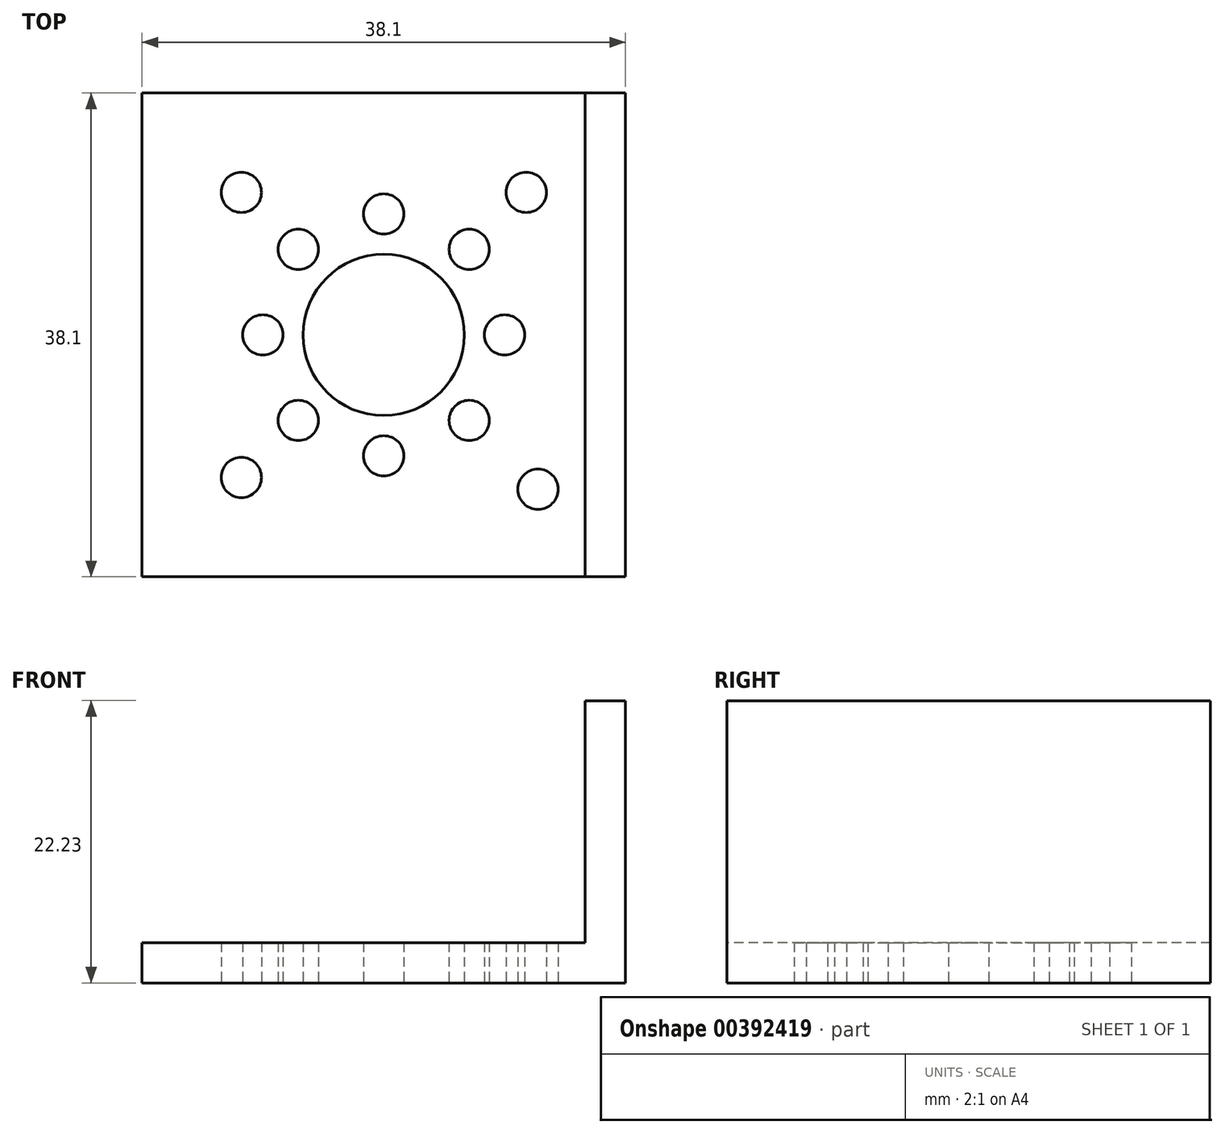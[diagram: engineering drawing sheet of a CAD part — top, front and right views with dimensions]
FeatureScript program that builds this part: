
annotation { "Feature Type Name" : "Feature", "Feature Type Description" : "" }
export const myFeature = defineFeature(function(context is Context, id is Id, definition is map)
    precondition{}
    {
        {
            var Q0;
            Q0=qCreatedBy(makeId("Top.planeOp"),FACE);
            var sketch = newSketch(context, id + "F0", { "sketchPlane" : qUnion([Q0])});
            skLineSegment(sketch, "E0.bottom", {"start": v(-38.1, 48.74) * mm, "end": v(0, 48.74) * mm});
            skLineSegment(sketch, "E0.top", {"start": v(-38.1, 10.64) * mm, "end": v(0, 10.64) * mm});
            skLineSegment(sketch, "E0.left", {"start": v(-38.1, 48.74) * mm, "end": v(-38.1, 10.64) * mm});
            skLineSegment(sketch, "E0.right", {"start": v(0, 48.74) * mm, "end": v(0, 10.64) * mm});
            skLineSegment(sketch, "E1.bottom", {"start": v(0, 48.74) * mm, "end": v(0, 48.74) * mm});
            skLineSegment(sketch, "E1.top", {"start": v(0, 10.64) * mm, "end": v(0, 10.64) * mm});
            skLineSegment(sketch, "E2.left", {"start": v(0, 10.64) * mm, "end": v(0, 48.74) * mm});
            skCircle(sketch, "E3", {"center": v(-19.05, 29.7) * mm, "radius": 6.35 * mm});
            skCircle(sketch, "E4", {"center": v(-19.05, 20.17) * mm, "radius": 1.59 * mm});
            skPoint(sketch, "E5", {"position": v(-19.05, 10.64) * mm});
            skPoint(sketch, "E6", {"position": v(-19.05, 48.74) * mm});
            skPoint(sketch, "E7", {"position": v(-38.1, 29.7) * mm});
            skPoint(sketch, "E8", {"position": v(0, 29.7) * mm});
            skLineSegment(sketch, "E9", {"start": v(-19.05, 10.64) * mm, "end": v(-19.05, 48.74) * mm});
            skLineSegment(sketch, "E10", {"start": v(0, 29.7) * mm, "end": v(-38.1, 29.7) * mm});
            skLineSegment(sketch, "E11", {"start": v(-38.1, 48.74) * mm, "end": v(0, 10.64) * mm});
            skLineSegment(sketch, "E12", {"start": v(0, 48.74) * mm, "end": v(-38.1, 10.64) * mm});
            skPoint(sketch, "E13", {"position": v(-19.05, 23.34) * mm});
            skPoint(sketch, "E14", {"position": v(-19.05, 36.04) * mm});
            skCircle(sketch, "E15", {"center": v(-19.05, 39.22) * mm, "radius": 1.59 * mm});
            skCircle(sketch, "E16", {"center": v(-28.58, 29.7) * mm, "radius": 1.59 * mm});
            skCircle(sketch, "E17", {"center": v(-9.53, 29.7) * mm, "radius": 1.59 * mm});
            skCircle(sketch, "E18", {"center": v(-25.79, 22.96) * mm, "radius": 1.59 * mm});
            skCircle(sketch, "E19", {"center": v(-12.31, 36.43) * mm, "radius": 1.59 * mm});
            skCircle(sketch, "E20", {"center": v(-25.79, 36.43) * mm, "radius": 1.59 * mm});
            skCircle(sketch, "E21", {"center": v(-12.31, 22.96) * mm, "radius": 1.59 * mm});
            skCircle(sketch, "E22", {"center": v(-30.28, 18.47) * mm, "radius": 1.59 * mm});
            skCircle(sketch, "E23", {"center": v(-6.9, 17.54) * mm, "radius": 1.59 * mm});
            skCircle(sketch, "E24", {"center": v(-30.28, 40.92) * mm, "radius": 1.59 * mm});
            skCircle(sketch, "E25", {"center": v(-7.82, 40.92) * mm, "radius": 1.59 * mm});
            skPoint(sketch, "E26", {"position": v(-23.54, 25.2) * mm});
            skPoint(sketch, "E27", {"position": v(-14.56, 25.2) * mm});
            skPoint(sketch, "E28", {"position": v(-25.4, 29.7) * mm});
            skPoint(sketch, "E29", {"position": v(-23.54, 34.18) * mm});
            skPoint(sketch, "E30", {"position": v(-14.56, 34.18) * mm});
            skPoint(sketch, "E31", {"position": v(-12.7, 29.7) * mm});
            skPoint(sketch, "E32", {"position": v(-26.9, 21.83) * mm});
            skPoint(sketch, "E33", {"position": v(-29.15, 19.59) * mm});
            skPoint(sketch, "E34", {"position": v(-11.2, 21.83) * mm});
            skPoint(sketch, "E35", {"position": v(-8.02, 18.66) * mm});
            skPoint(sketch, "E36", {"position": v(-11.2, 37.55) * mm});
            skPoint(sketch, "E37", {"position": v(-8.95, 39.8) * mm});
            skPoint(sketch, "E38", {"position": v(-29.15, 39.8) * mm});
            skPoint(sketch, "E39", {"position": v(-26.9, 37.55) * mm});
            skPoint(sketch, "E2.right.end.orphan", {"position": v(3.17, 48.74) * mm});
            skSolve(sketch);
        }
        {
            var Q0;
            {var subQ0=sQuery(id+"F0.wireOp",EDGE,"E10");var subQ1=sQuery(id+"F0.wireOp",EDGE,"E3");var subQ2=makeQuery(id+"F0.imprint","INTERSECT",VERTEX,{"disambiguationData":[OD(0.0)],"derivedFrom":[subQ1,subQ0]});Q0=makeQuery(id+"F0.imprint","IMPRINT",FACE,{"disambiguationData":[TD([[makeQuery(id+"F0.imprint","IMPRINT",EDGE,{"disambiguationData":[TD([[subQ2,1.0]])],"derivedFrom":subQ1}),-1.0]])]});}
            var Q1;
            {var subQ0=sQuery(id+"F0.wireOp",EDGE,"E9");var subQ6=sQuery(id+"F0.wireOp",EDGE,"E3");var subQ7=makeQuery(id+"F0.imprint","INTERSECT",VERTEX,{"disambiguationData":[OD(1.0)],"derivedFrom":[subQ6,subQ0]});Q1=makeQuery(id+"F0.imprint","IMPRINT",FACE,{"disambiguationData":[TD([[makeQuery(id+"F0.imprint","IMPRINT",EDGE,{"disambiguationData":[TD([[subQ7,-1.0]])],"derivedFrom":subQ6}),-1.0]])]});}
            var Q2;
            {var subQ7=sQuery(id+"F0.wireOp",EDGE,"E12");var subQ10=sQuery(id+"F0.wireOp",EDGE,"E3");var subQ11=makeQuery(id+"F0.imprint","INTERSECT",VERTEX,{"disambiguationData":[OD(1.0)],"derivedFrom":[subQ10,subQ7]});Q2=makeQuery(id+"F0.imprint","IMPRINT",FACE,{"disambiguationData":[TD([[makeQuery(id+"F0.imprint","IMPRINT",EDGE,{"disambiguationData":[TD([[subQ11,-1.0]])],"derivedFrom":subQ10}),-1.0]])]});}
            var Q3;
            {var subQ0=sQuery(id+"F0.wireOp",EDGE,"E10");var subQ10=sQuery(id+"F0.wireOp",EDGE,"E3");var subQ11=makeQuery(id+"F0.imprint","INTERSECT",VERTEX,{"disambiguationData":[OD(1.0)],"derivedFrom":[subQ10,subQ0]});Q3=makeQuery(id+"F0.imprint","IMPRINT",FACE,{"disambiguationData":[TD([[makeQuery(id+"F0.imprint","IMPRINT",EDGE,{"disambiguationData":[TD([[subQ11,-1.0]])],"derivedFrom":subQ10}),-1.0]])]});}
            var Q4;
            {var subQ5=sQuery(id+"F0.wireOp",EDGE,"E11");var subQ6=sQuery(id+"F0.wireOp",EDGE,"E3");var subQ7=makeQuery(id+"F0.imprint","INTERSECT",VERTEX,{"disambiguationData":[OD(0.0)],"derivedFrom":[subQ6,subQ5]});Q4=makeQuery(id+"F0.imprint","IMPRINT",FACE,{"disambiguationData":[TD([[makeQuery(id+"F0.imprint","IMPRINT",EDGE,{"disambiguationData":[TD([[subQ7,-1.0]])],"derivedFrom":subQ6}),-1.0]])]});}
            var Q5;
            {var subQ0=sQuery(id+"F0.wireOp",EDGE,"E9");var subQ1=sQuery(id+"F0.wireOp",EDGE,"E3");var subQ2=makeQuery(id+"F0.imprint","INTERSECT",VERTEX,{"disambiguationData":[OD(0.0)],"derivedFrom":[subQ1,subQ0]});Q5=makeQuery(id+"F0.imprint","IMPRINT",FACE,{"disambiguationData":[TD([[makeQuery(id+"F0.imprint","IMPRINT",EDGE,{"disambiguationData":[TD([[subQ2,-1.0]])],"derivedFrom":subQ1}),-1.0]])]});}
            var Q6;
            {var subQ5=sQuery(id+"F0.wireOp",EDGE,"E12");var subQ6=sQuery(id+"F0.wireOp",EDGE,"E3");var subQ7=makeQuery(id+"F0.imprint","INTERSECT",VERTEX,{"disambiguationData":[OD(0.0)],"derivedFrom":[subQ6,subQ5]});Q6=makeQuery(id+"F0.imprint","IMPRINT",FACE,{"disambiguationData":[TD([[makeQuery(id+"F0.imprint","IMPRINT",EDGE,{"disambiguationData":[TD([[subQ7,-1.0]])],"derivedFrom":subQ6}),-1.0]])]});}
            var Q7;
            {var subQ1=sQuery(id+"F0.wireOp",EDGE,"E3");var subQ5=sQuery(id+"F0.wireOp",EDGE,"E12");var subQ9=makeQuery(id+"F0.imprint","INTERSECT",VERTEX,{"disambiguationData":[OD(0.0)],"derivedFrom":[subQ1,subQ5]});Q7=makeQuery(id+"F0.imprint","IMPRINT",FACE,{"disambiguationData":[TD([[makeQuery(id+"F0.imprint","IMPRINT",EDGE,{"disambiguationData":[TD([[subQ9,1.0]])],"derivedFrom":subQ1}),-1.0]])]});}
            extrude(context, id + "F1", {"entities" : qUnion([Q0, Q1, Q2, Q3, Q4, Q5, Q6, Q7]), "depth" : 3.17 * mm});
        }
        {
            var Q0;
            Q0=makeQuery(id+"F1.opExtrude","CAP_FACE",FACE,{"disambiguationData":[OSD([sQuery(id+"F0.wireOp",EDGE,"E0.bottom"),sQuery(id+"F0.wireOp",EDGE,"E0.top"),sQuery(id+"F0.wireOp",EDGE,"E0.left"),sQuery(id+"F0.wireOp",EDGE,"E2.left"),sQuery(id+"F0.wireOp",EDGE,"E3"),sQuery(id+"F0.wireOp",EDGE,"E4"),sQuery(id+"F0.wireOp",EDGE,"E15"),sQuery(id+"F0.wireOp",EDGE,"E16"),sQuery(id+"F0.wireOp",EDGE,"E17"),sQuery(id+"F0.wireOp",EDGE,"E18"),sQuery(id+"F0.wireOp",EDGE,"E19"),sQuery(id+"F0.wireOp",EDGE,"E20"),sQuery(id+"F0.wireOp",EDGE,"E21"),sQuery(id+"F0.wireOp",EDGE,"E22"),sQuery(id+"F0.wireOp",EDGE,"E23"),sQuery(id+"F0.wireOp",EDGE,"E24"),sQuery(id+"F0.wireOp",EDGE,"E25")])],"isStart":false});
            var sketch = newSketch(context, id + "F2", { "sketchPlane" : qUnion([Q0])});
            skLineSegment(sketch, "E40.bottom", {"start": v(0, 48.74) * mm, "end": v(-3.18, 48.74) * mm});
            skLineSegment(sketch, "E40.top", {"start": v(0, 10.64) * mm, "end": v(-3.17, 10.64) * mm});
            skLineSegment(sketch, "E40.left", {"start": v(0, 48.74) * mm, "end": v(0, 10.64) * mm});
            skLineSegment(sketch, "E40.right", {"start": v(-3.18, 48.74) * mm, "end": v(-3.17, 10.64) * mm});
            skSolve(sketch);
        }
        {
            var Q0;
            Q0=makeQuery(id+"F2.imprint","IMPRINT",FACE,{"disambiguationData":[TD([[makeQuery(id+"F2.imprint","IMPRINT",EDGE,{"derivedFrom":sQuery(id+"F2.wireOp",EDGE,"E40.bottom")}),-1.0]])]});
            extrude(context, id + "F3", {"entities" : qUnion([Q0]), "operationType" : NewBodyOperationType.ADD, "depth" : 19.05 * mm});
        }
    });
